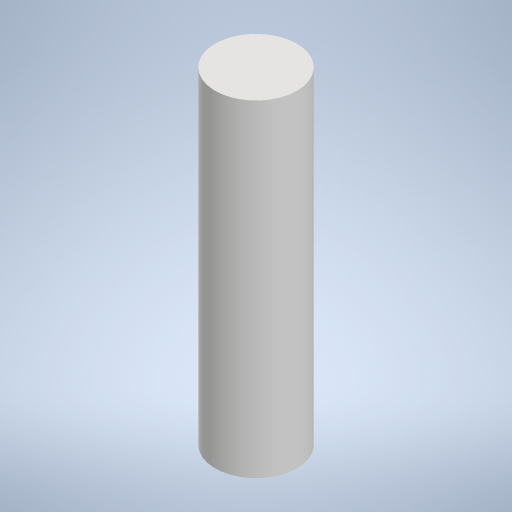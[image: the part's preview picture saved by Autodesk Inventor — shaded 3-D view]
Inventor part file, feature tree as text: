
AUTODESK INVENTOR PART (.ipt)
format: ipt  version: 2024.2 (Build 282272000, 272)  size: 214,528 bytes
history: native  units: mm
features: extrude x1, sketch x1
ambient origin geometry x8: Origin, YZ Plane, XZ Plane, XY Plane, X Axis, Y Axis, Z Axis, Center Point
bodies: Solid1 (feature_tree)
feature tree (2):
  extrude  "Extrusion1"  Depth=450.0mm
  sketch  "Sketch1"  dims[d0=250.0mm d1=450.0mm d2=1000.0mm d3=0.0mm]
